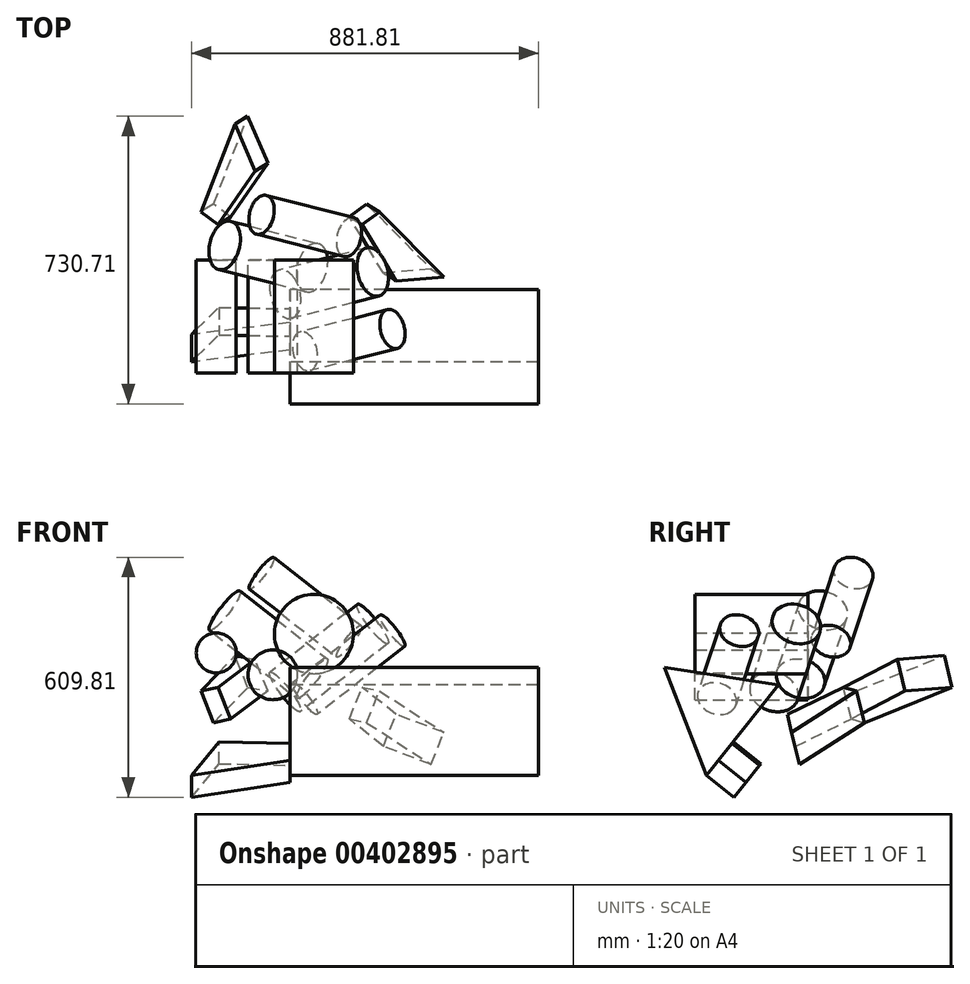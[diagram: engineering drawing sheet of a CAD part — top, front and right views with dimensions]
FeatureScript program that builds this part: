
annotation { "Feature Type Name" : "Feature", "Feature Type Description" : "" }
export const myFeature = defineFeature(function(context is Context, id is Id, definition is map)
    precondition{}
    {
        {
            var Q0;
            Q0=qCreatedBy(makeId("Front.planeOp"),FACE);
            var sketch = newSketch(context, id + "F0", { "sketchPlane" : qUnion([Q0])});
            skCircle(sketch, "E0", {"center": v(-43.57, 87.5) * mm, "radius": 63.1 * mm});
            skPoint(sketch, "E0.first.point", {"position": v(-101.42, 62.29) * mm});
            skPoint(sketch, "E0.second.point", {"position": v(-31.72, 149.5) * mm});
            skPoint(sketch, "E0.third.point", {"position": v(0, 41.85) * mm});
            skSolve(sketch);
        }
        {
            var Q0;
            Q0=qCreatedBy(makeId("Front.planeOp"),FACE);
            var sketch = newSketch(context, id + "F1", { "sketchPlane" : qUnion([Q0])});
            skCircle(sketch, "E1", {"center": v(60.54, 191.12) * mm, "radius": 100.58 * mm});
            skCircle(sketch, "E2", {"center": v(-187.47, 143.43) * mm, "radius": 50.72 * mm});
            skSolve(sketch);
        }
        {
            var Q0;
            Q0=makeQuery(id+"F1.imprint","IMPRINT",FACE,{"disambiguationData":[TD([[makeQuery(id+"F1.imprint","IMPRINT",EDGE,{"derivedFrom":sQuery(id+"F1.wireOp",EDGE,"E1")}),1.0]])]});
            var Q1;
            Q1=makeQuery(id+"F0.imprint","IMPRINT",FACE,{"disambiguationData":[TD([[makeQuery(id+"F0.imprint","IMPRINT",EDGE,{"derivedFrom":sQuery(id+"F0.wireOp",EDGE,"E0")}),1.0]])]});
            var Q2;
            Q2=makeQuery(id+"F1.imprint","IMPRINT",FACE,{"disambiguationData":[TD([[makeQuery(id+"F1.imprint","IMPRINT",EDGE,{"derivedFrom":sQuery(id+"F1.wireOp",EDGE,"E2")}),1.0]])]});
            var Q3;
            Q3 = qSketchRegion(id + "F1", true);
            extrude(context, id + "F2", {"entities" : qUnion([Q0, Q1, Q2, Q3]), "depth" : 287 * mm});
        }
        {
            var Q0;
            Q0=qCreatedBy(makeId("Right.planeOp"),FACE);
            var sketch = newSketch(context, id + "F3", { "sketchPlane" : qUnion([Q0])});
            skLineSegment(sketch, "E3", {"start": v(0, 0) * mm, "end": v(-166.74, 331.55) * mm});
            skLineSegment(sketch, "E4", {"start": v(-166.74, 331.55) * mm, "end": v(-304.58, 331.55) * mm});
            skSolve(sketch);
        }
        {
            var Q0;
            Q0=qCreatedBy(makeId("Right.planeOp"),FACE);
            var sketch = newSketch(context, id + "F4", { "sketchPlane" : qUnion([Q0])});
            skCircle(sketch, "E5.cCircle", {"center": v(-232.67, 0) * mm, "radius": 169.51 * mm, "construction": true});
            skLineSegment(sketch, "E5.0", {"start": v(-258.48, -167.54) * mm, "end": v(-364.86, 106.12) * mm});
            skLineSegment(sketch, "E5.1", {"start": v(-364.86, 106.12) * mm, "end": v(-74.68, 61.42) * mm});
            skLineSegment(sketch, "E5.2", {"start": v(-74.68, 61.42) * mm, "end": v(-258.48, -167.54) * mm});
            skSolve(sketch);
        }
        {
            var Q0;
            Q0=makeQuery(id+"F4.imprint","IMPRINT",FACE,{"disambiguationData":[TD([[makeQuery(id+"F4.imprint","IMPRINT",EDGE,{"derivedFrom":sQuery(id+"F4.wireOp",EDGE,"E5.0")}),-1.0]])]});
            extrude(context, id + "F5", {"entities" : qUnion([Q0]), "depth" : 631.03 * mm});
        }
        {
            var Q0;
            Q0=makeQuery(id+"F5.opExtrude","SWEPT_FACE",FACE,{"disambiguationData":[OSD([sQuery(id+"F4.wireOp",EDGE,"E5.2")])]});
            var sketch = newSketch(context, id + "F6", { "sketchPlane" : qUnion([Q0])});
            skLineSegment(sketch, "E6", {"start": v(-248.8, -195.15) * mm, "end": v(250.78, -292.46) * mm});
            skPoint(sketch, "E6.endSnap0", {"position": v(-315.51, -292.46) * mm});
            skLineSegment(sketch, "E7", {"start": v(250.78, -292.46) * mm, "end": v(180.39, -183.03) * mm});
            skLineSegment(sketch, "E8", {"start": v(180.39, -183.03) * mm, "end": v(-248.8, -195.15) * mm});
            skSolve(sketch);
        }
        {
            var Q0;
            {var subQ0=sQuery(id+"F6.wireOp",EDGE,"E7");Q0=makeQuery(id+"F6.imprint","IMPRINT",FACE,{"disambiguationData":[TD([[makeQuery(id+"F6.imprint","IMPRINT",EDGE,{"derivedFrom":subQ0}),1.0]])]});}
            extrude(context, id + "F7", {"entities" : qUnion([Q0]), "depth" : 89.52 * mm});
        }
        {
            var Q0;
            Q0=makeQuery(id+"F7.opExtrude","SWEPT_BODY",BODY,{"disambiguationData":[OSD([sQuery(id+"F4.wireOp",EDGE,"E5.2"),sQuery(id+"F6.wireOp",EDGE,"E6"),sQuery(id+"F6.wireOp",EDGE,"E7"),sQuery(id+"F6.wireOp",EDGE,"E8")])]});
            var Q1;
            Q1=makeQuery(id+"F2.opExtrude","SWEPT_BODY",BODY,{"disambiguationData":[OSD([sQuery(id+"F0.wireOp",EDGE,"E0")])]});
            var Q2;
            Q2=makeQuery(id+"F2.opExtrude","SWEPT_BODY",BODY,{"disambiguationData":[OSD([sQuery(id+"F1.wireOp",EDGE,"E2")])]});
            var Q3;
            Q3=sQuery(id+"F3.wireOp",EDGE,"E3");
            circularPattern(context, id + "F8", {"entities" : qUnion([Q0, Q1, Q2]), "axis" : qUnion([Q3]), "angle" : 360 * degree, "instanceCount" : 3, "equalSpace" : true});
        }
    });
